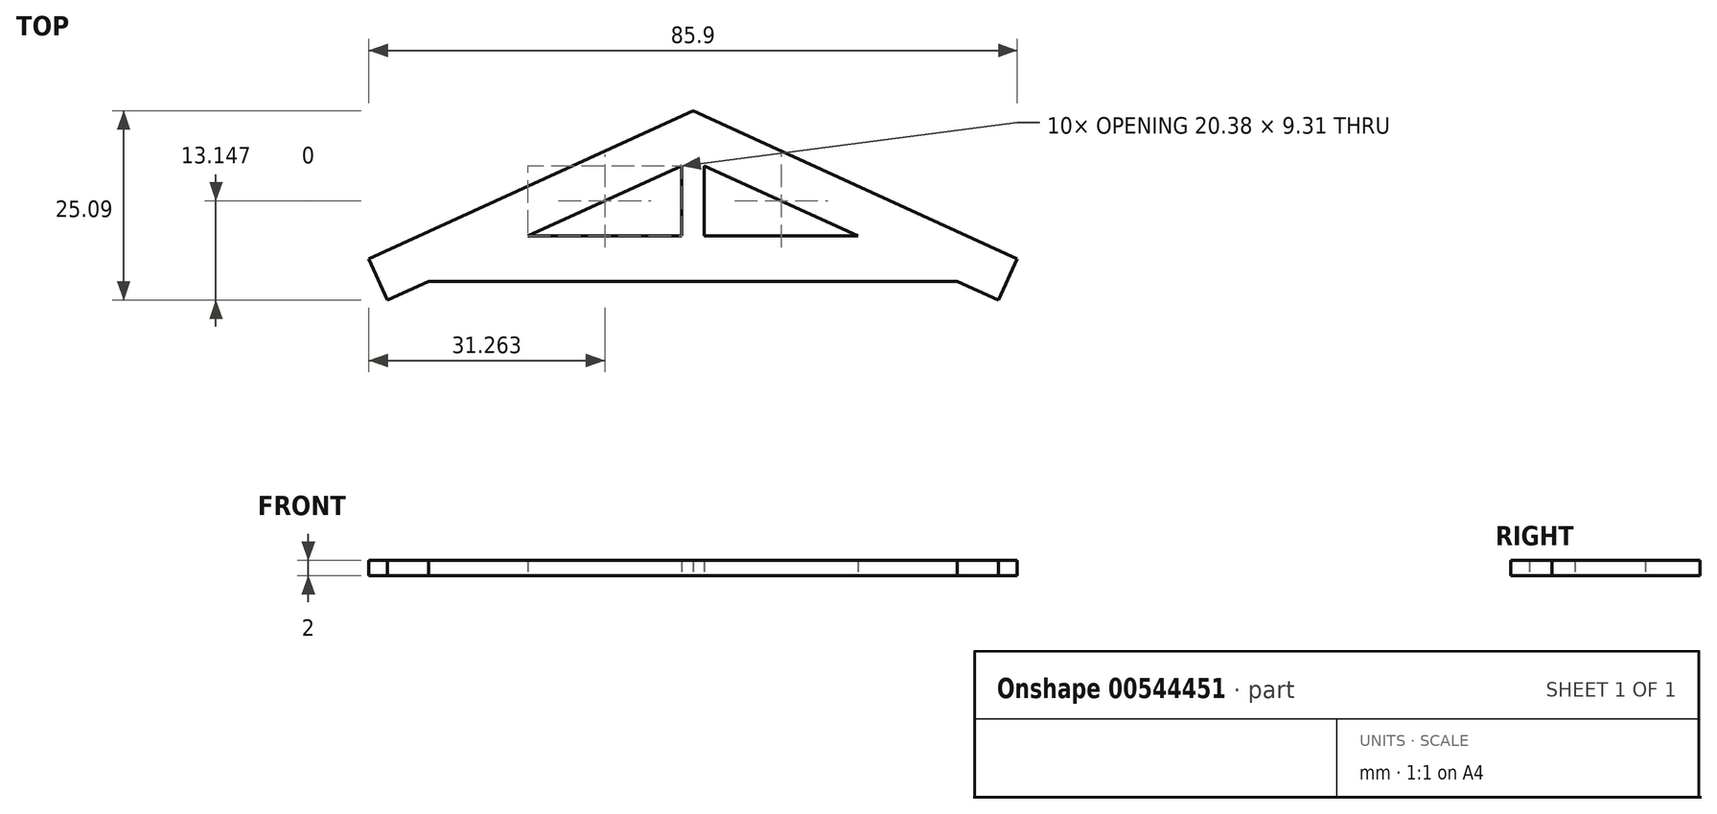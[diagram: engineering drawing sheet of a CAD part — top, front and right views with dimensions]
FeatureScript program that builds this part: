
annotation { "Feature Type Name" : "Feature", "Feature Type Description" : "" }
export const myFeature = defineFeature(function(context is Context, id is Id, definition is map)
    precondition{}
    {
        {
            var Q0;
            Q0=qCreatedBy(makeId("Top.planeOp"),FACE);
            var sketch = newSketch(context, id + "F0", { "sketchPlane" : qUnion([Q0])});
            skLineSegment(sketch, "E0", {"start": v(0, 0) * mm, "end": v(35, 0) * mm});
            skLineSegment(sketch, "E1.MirrorCS", {"start": v(0, 0) * mm, "end": v(-35, 0) * mm});
            skLineSegment(sketch, "E2", {"start": v(1.5, 15.31) * mm, "end": v(21.88, 6) * mm});
            skLineSegment(sketch, "E3", {"start": v(-1.5, 15.31) * mm, "end": v(-21.88, 6) * mm});
            skLineSegment(sketch, "E4.0", {"start": v(1.5, 6) * mm, "end": v(1.5, 15.31) * mm});
            skLineSegment(sketch, "E5.0", {"start": v(-1.5, 6) * mm, "end": v(-1.5, 15.31) * mm});
            skLineSegment(sketch, "E6.0", {"start": v(0, 22.6) * mm, "end": v(-37.5, 5.46) * mm});
            skLineSegment(sketch, "E6.1", {"start": v(0, 22.6) * mm, "end": v(37.5, 5.46) * mm});
            skLineSegment(sketch, "E7", {"start": v(35, 0) * mm, "end": v(40.46, -2.5) * mm});
            skLineSegment(sketch, "E8.MirrorCS", {"start": v(-35, 0) * mm, "end": v(-40.46, -2.5) * mm});
            skLineSegment(sketch, "E9", {"start": v(37.5, 5.46) * mm, "end": v(42.95, 2.96) * mm});
            skLineSegment(sketch, "E10.MirrorCS", {"start": v(-37.5, 5.46) * mm, "end": v(-42.95, 2.96) * mm});
            skLineSegment(sketch, "E11", {"start": v(-42.95, 2.96) * mm, "end": v(-40.46, -2.5) * mm});
            skLineSegment(sketch, "E12", {"start": v(40.46, -2.5) * mm, "end": v(42.95, 2.96) * mm});
            skLineSegment(sketch, "E13.0", {"start": v(-1.5, 6) * mm, "end": v(-21.88, 6) * mm});
            skLineSegment(sketch, "E14.MirrorCS", {"start": v(1.5, 6) * mm, "end": v(21.88, 6) * mm});
            skPoint(sketch, "E15.orphan", {"position": v(35, 6) * mm});
            skPoint(sketch, "E16.orphan", {"position": v(-35, 6) * mm});
            skPoint(sketch, "E17.orphan", {"position": v(0, 6) * mm});
            skSolve(sketch);
        }
        {
            var Q0;
            Q0 = qSketchRegion(id + "F0", true);
            extrude(context, id + "F1", {"entities" : qUnion([Q0]), "depth" : 2 * mm, "offsetDistance" : 25 * mm});
        }
    });
